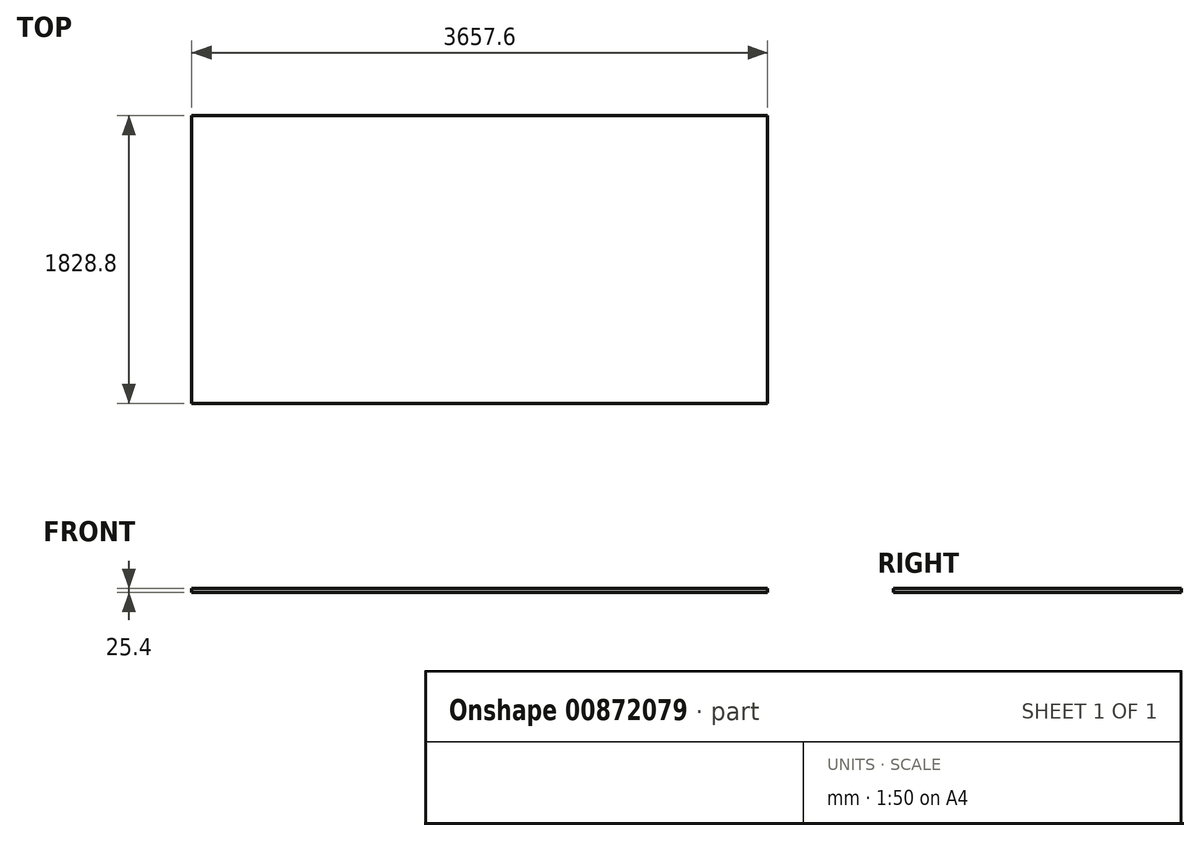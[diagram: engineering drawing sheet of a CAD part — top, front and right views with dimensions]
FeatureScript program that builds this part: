
annotation { "Feature Type Name" : "Feature", "Feature Type Description" : "" }
export const myFeature = defineFeature(function(context is Context, id is Id, definition is map)
    precondition{}
    {
        {
            var Q0;
            Q0=qCreatedBy(makeId("Top.planeOp"),FACE);
            var sketch = newSketch(context, id + "F0", { "sketchPlane" : qUnion([Q0])});
            skLineSegment(sketch, "E0.bottom", {"start": v(0, 0) * mm, "end": v(3657.6, 0) * mm});
            skLineSegment(sketch, "E0.top", {"start": v(0, 1828.8) * mm, "end": v(3657.6, 1828.8) * mm});
            skLineSegment(sketch, "E0.left", {"start": v(0, 0) * mm, "end": v(0, 1828.8) * mm});
            skLineSegment(sketch, "E0.right", {"start": v(3657.6, 0) * mm, "end": v(3657.6, 1828.8) * mm});
            skSolve(sketch);
        }
        {
            var Q0;
            Q0=qSketchRegion(id+"F0",true);
            extrude(context, id + "F1", {"entities" : qUnion([Q0]), "depth" : 25.4 * mm});
        }
    });
